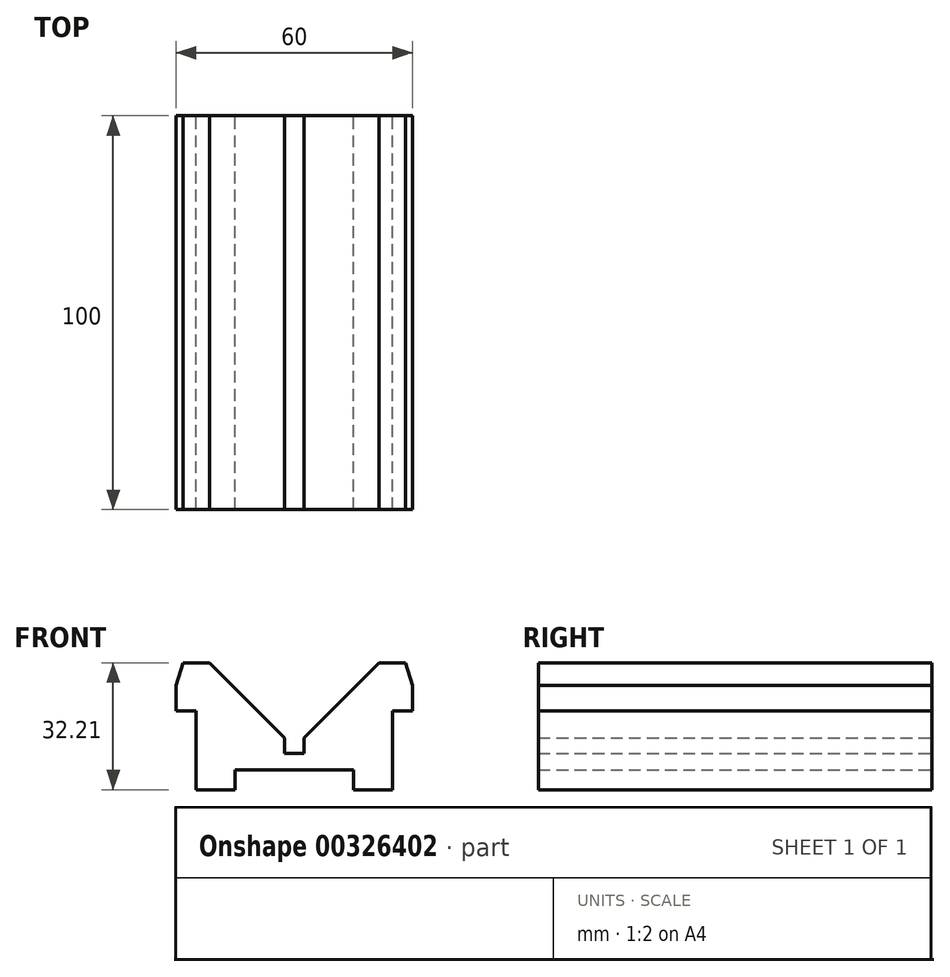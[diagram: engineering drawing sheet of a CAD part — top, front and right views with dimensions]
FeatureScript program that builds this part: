
annotation { "Feature Type Name" : "Feature", "Feature Type Description" : "" }
export const myFeature = defineFeature(function(context is Context, id is Id, definition is map)
    precondition{}
    {
        {
            var Q0;
            Q0=qCreatedBy(makeId("Front.planeOp"),FACE);
            var sketch = newSketch(context, id + "F0", { "sketchPlane" : qUnion([Q0])});
            skLineSegment(sketch, "E0", {"start": v(0, 64.17) * mm, "end": v(0, -61.83) * mm, "construction": true});
            skLineSegment(sketch, "E1", {"start": v(0, 25.78) * mm, "end": v(-2.5, 25.78) * mm});
            skLineSegment(sketch, "E2", {"start": v(-2.5, 25.78) * mm, "end": v(-2.5, 29.78) * mm});
            skLineSegment(sketch, "E3", {"start": v(-2.5, 29.78) * mm, "end": v(-21.5, 48.78) * mm});
            skLineSegment(sketch, "E4", {"start": v(-21.5, 48.78) * mm, "end": v(-28.28, 48.78) * mm});
            skLineSegment(sketch, "E5", {"start": v(-28.28, 48.78) * mm, "end": v(-30, 43.03) * mm});
            skLineSegment(sketch, "E6", {"start": v(-30, 43.03) * mm, "end": v(-30, 36.57) * mm});
            skLineSegment(sketch, "E7", {"start": v(-30, 36.57) * mm, "end": v(-25, 36.57) * mm});
            skLineSegment(sketch, "E8", {"start": v(-25, 36.57) * mm, "end": v(-25, 16.57) * mm});
            skLineSegment(sketch, "E9", {"start": v(-25, 16.57) * mm, "end": v(-15, 16.57) * mm});
            skLineSegment(sketch, "E10", {"start": v(-15, 16.57) * mm, "end": v(-15, 21.57) * mm});
            skLineSegment(sketch, "E11", {"start": v(-15, 21.57) * mm, "end": v(0, 21.57) * mm});
            skLineSegment(sketch, "E12.MirrorCS", {"start": v(2.5, 29.78) * mm, "end": v(21.5, 48.78) * mm});
            skLineSegment(sketch, "E13.MirrorCS", {"start": v(21.5, 48.78) * mm, "end": v(28.28, 48.78) * mm});
            skLineSegment(sketch, "E14.MirrorCS", {"start": v(28.28, 48.78) * mm, "end": v(30, 43.03) * mm});
            skLineSegment(sketch, "E15.MirrorCS", {"start": v(30, 43.03) * mm, "end": v(30, 36.57) * mm});
            skLineSegment(sketch, "E16.MirrorCS", {"start": v(30, 36.57) * mm, "end": v(25, 36.57) * mm});
            skLineSegment(sketch, "E17.MirrorCS", {"start": v(25, 36.57) * mm, "end": v(25, 16.57) * mm});
            skLineSegment(sketch, "E18.MirrorCS", {"start": v(25, 16.57) * mm, "end": v(15, 16.57) * mm});
            skLineSegment(sketch, "E19.MirrorCS", {"start": v(15, 16.57) * mm, "end": v(15, 21.57) * mm});
            skLineSegment(sketch, "E20.MirrorCS", {"start": v(15, 21.57) * mm, "end": v(0, 21.57) * mm});
            skLineSegment(sketch, "E21.MirrorCS", {"start": v(0, 25.78) * mm, "end": v(2.5, 25.78) * mm});
            skLineSegment(sketch, "E22.MirrorCS", {"start": v(2.5, 25.78) * mm, "end": v(2.5, 29.78) * mm});
            skSolve(sketch);
        }
        {
            var Q0;
            Q0 = qSketchRegion(id + "F0", true);
            extrude(context, id + "F1", {"entities" : qUnion([Q0]), "depth" : 100 * mm});
        }
    });
